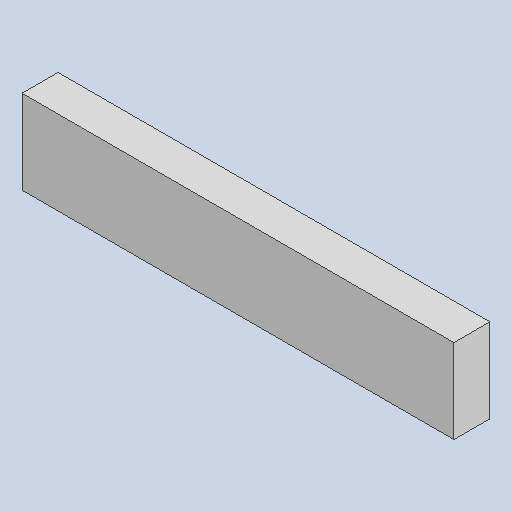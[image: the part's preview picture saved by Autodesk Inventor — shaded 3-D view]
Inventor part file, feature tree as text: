
AUTODESK INVENTOR PART (.ipt)
format: ipt  version: 2025 (Build 290162000, 162)  size: 80,384 bytes
history: native  units: in
note: dims shown in document units (in); Inventor stores cm internally (conversion verified against a paired STEP export)
features: other x3, sketch x1
ambient origin geometry x8: Origin, YZ Plane, XZ Plane, XY Plane, X Axis, Y Axis, Z Axis, Center Point
bodies: Solid1 (feature_tree)
feature tree (4):
  other  "back-side_MIR.ipt"
  other  "Solid1::back-side_MIR.ipt"
  other  "TaggingFeature1"
  sketch  "Sketch1"  dims[d0=0.3937in]
